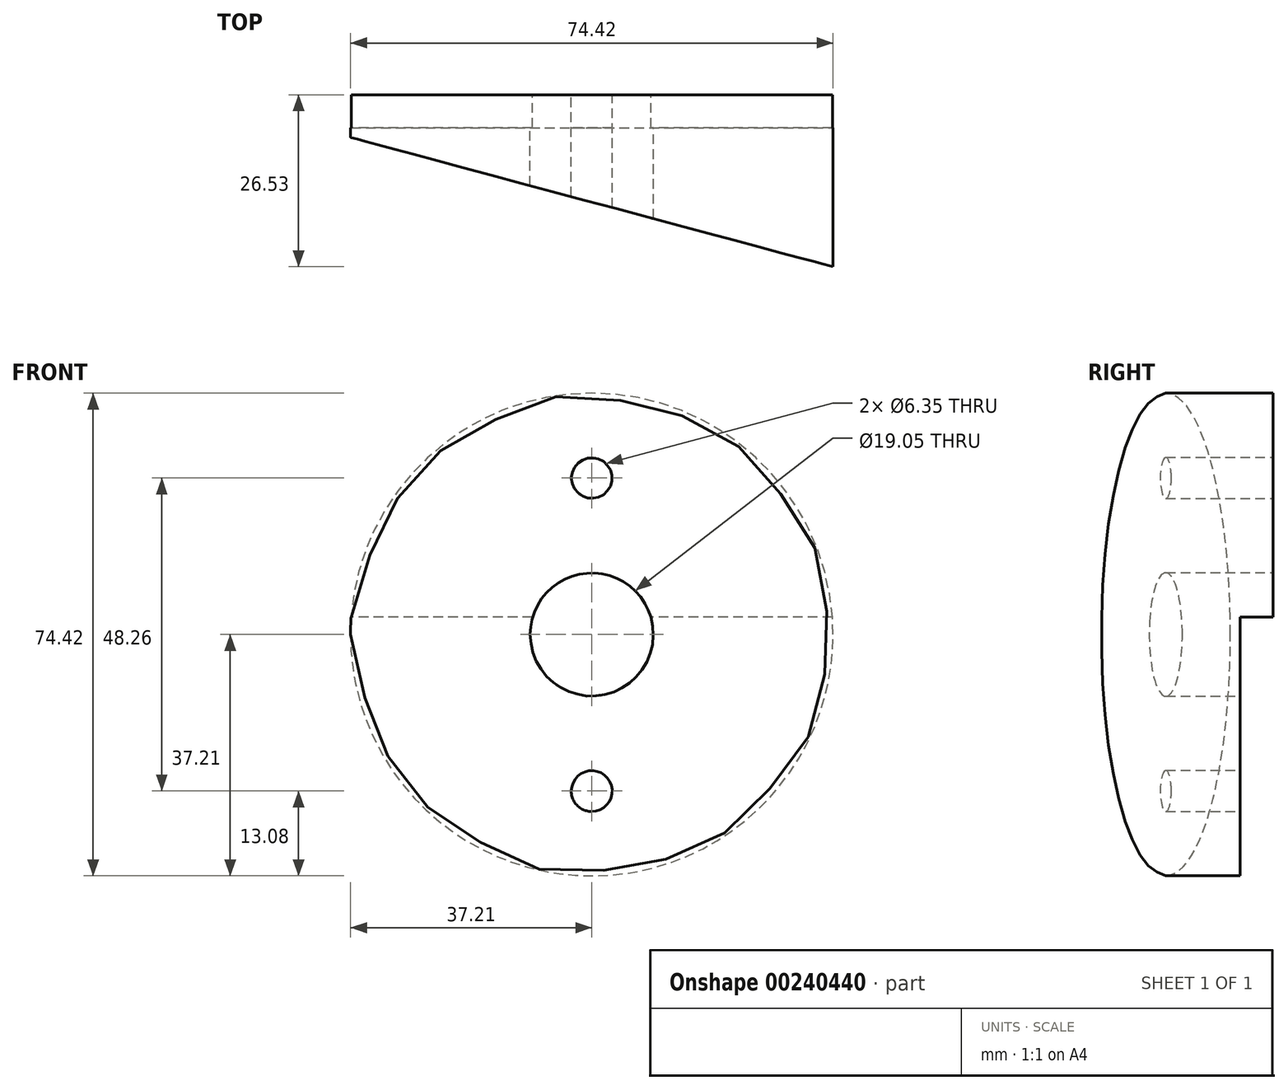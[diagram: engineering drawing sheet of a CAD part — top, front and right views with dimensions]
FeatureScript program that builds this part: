
annotation { "Feature Type Name" : "Feature", "Feature Type Description" : "" }
export const myFeature = defineFeature(function(context is Context, id is Id, definition is map)
    precondition{}
    {
        {
            var Q0;
            Q0=qCreatedBy(makeId("Front.planeOp"),FACE);
            var sketch = newSketch(context, id + "F0", { "sketchPlane" : qUnion([Q0])});
            skCircle(sketch, "E0", {"center": v(0, 0) * mm, "radius": 37.21 * mm});
            skCircle(sketch, "E1", {"center": v(0, 24.13) * mm, "radius": 3.18 * mm});
            skCircle(sketch, "E2", {"center": v(0, 0) * mm, "radius": 24.13 * mm, "construction": true});
            skCircle(sketch, "E3", {"center": v(0, 0) * mm, "radius": 9.53 * mm});
            skSolve(sketch);
        }
        {
            var Q0;
            Q0=makeQuery(id+"F0.imprint","IMPRINT",FACE,{"disambiguationData":[TD([[makeQuery(id+"F0.imprint","IMPRINT",EDGE,{"derivedFrom":sQuery(id+"F0.wireOp",EDGE,"E0")}),1.0]])]});
            var Q1;
            Q1=makeQuery(id+"F0.imprint","IMPRINT",FACE,{"disambiguationData":[TD([[makeQuery(id+"F0.imprint","IMPRINT",EDGE,{"derivedFrom":sQuery(id+"F0.wireOp",EDGE,"E1")}),-1.0]])]});
            extrude(context, id + "F1", {"entities" : qUnion([Q0, Q1]), "flatOperationType" : FlatOperationType.REMOVE, "offsetDistance" : 25.4 * mm, "depth" : 31.75 * mm, "domain" : OperationDomain.MODEL});
        }
        {
            var Q0;
            Q0=makeQuery(id+"F1.opExtrude","CAP_FACE",FACE,{"disambiguationData":[OSD([sQuery(id+"F0.wireOp",EDGE,"E0"),sQuery(id+"F0.wireOp",EDGE,"E1"),sQuery(id+"F0.wireOp",EDGE,"E3")])],"isStart":false});
            var sketch = newSketch(context, id + "F2", { "sketchPlane" : qUnion([Q0])});
            skCircle(sketch, "E4", {"center": v(0, 24.13) * mm, "radius": 4.45 * mm});
            skSolve(sketch);
        }
        {
            var Q0;
            Q0=makeQuery(id+"FjNrPwOApxwwvlc_1.boolean.opBoolean","COPY",FACE,{"derivedFrom":makeQuery(id+"FjNrPwOApxwwvlc_1.opExtrude","SWEPT_FACE",FACE,{"disambiguationData":[OSD([sQuery(id+"F2.wireOp",EDGE,"E4")])]})});
            var Q1;
            Q1=makeQuery(id+"F1.opExtrude","SWEPT_FACE",FACE,{"disambiguationData":[OSD([sQuery(id+"F0.wireOp",EDGE,"E1")])]});
            var Q2;
            Q2=makeQuery(id+"FjNrPwOApxwwvlc_1.boolean.opBoolean","COPY",FACE,{"derivedFrom":makeQuery(id+"FjNrPwOApxwwvlc_1.opExtrude","CAP_FACE",FACE,{"disambiguationData":[OSD([sQuery(id+"F2.wireOp",EDGE,"E4")])],"isStart":false})});
            var Q3;
            Q3=makeQuery(id+"F1.opExtrude","SWEPT_FACE",FACE,{"disambiguationData":[OSD([sQuery(id+"F0.wireOp",EDGE,"E3")])]});
            circularPattern(context, id + "F3", {"patternType" : PatternType.FACE, "faces" : qUnion([Q0, Q1, Q2]), "axis" : qUnion([Q3]), "angle" : 360 * degree, "instanceCount" : 2, "equalSpace" : true, "fullFeaturePattern" : false});
        }
        {
            var Q0;
            Q0=qCreatedBy(makeId("Top.planeOp"),FACE);
            var sketch = newSketch(context, id + "F4", { "sketchPlane" : qUnion([Q0])});
            skLineSegment(sketch, "E5", {"start": v(-38.1, -6.35) * mm, "end": v(56.7, -31.75) * mm});
            skLineSegment(sketch, "E6", {"start": v(-38.1, -6.35) * mm, "end": v(-38.1, -31.75) * mm});
            skLineSegment(sketch, "E7", {"start": v(56.7, -31.75) * mm, "end": v(-38.1, -31.75) * mm});
            skSolve(sketch);
        }
        {
            var Q0;
            Q0=makeQuery(id+"F4.imprint","IMPRINT",FACE,{"disambiguationData":[TD([[makeQuery(id+"F4.imprint","IMPRINT",EDGE,{"derivedFrom":sQuery(id+"F4.wireOp",EDGE,"E5")}),-1.0]])]});
            extrude(context, id + "F5", {"entities" : qUnion([Q0]), "operationType" : NewBodyOperationType.REMOVE, "endBound" : BoundingType.SYMMETRIC, "depth" : 92.46 * mm});
        }
        {
            var Q0;
            Q0=qCreatedBy(makeId("Front.planeOp"),FACE);
            var sketch = newSketch(context, id + "F6", { "sketchPlane" : qUnion([Q0])});
            skLineSegment(sketch, "E8.bottom", {"start": v(50.8, 2.67) * mm, "end": v(-50.8, 2.67) * mm});
            skLineSegment(sketch, "E8.top", {"start": v(50.8, -48.13) * mm, "end": v(-50.8, -48.13) * mm});
            skLineSegment(sketch, "E8.left", {"start": v(50.8, 2.67) * mm, "end": v(50.8, -48.13) * mm});
            skLineSegment(sketch, "E8.right", {"start": v(-50.8, 2.67) * mm, "end": v(-50.8, -48.13) * mm});
            skLineSegment(sketch, "E9", {"start": v(0, 2.67) * mm, "end": v(0, -48.13) * mm, "construction": true});
            skSolve(sketch);
        }
        {
            var Q0;
            Q0=makeQuery(id+"F6.imprint","IMPRINT",FACE,{"disambiguationData":[TD([[makeQuery(id+"F6.imprint","IMPRINT",EDGE,{"derivedFrom":sQuery(id+"F6.wireOp",EDGE,"E8.bottom")}),1.0]])]});
            extrude(context, id + "F7", {"entities" : qUnion([Q0]), "operationType" : NewBodyOperationType.REMOVE, "flatOperationType" : FlatOperationType.REMOVE, "offsetDistance" : 25.4 * mm, "depth" : 5.08 * mm, "domain" : OperationDomain.MODEL});
        }
    });
